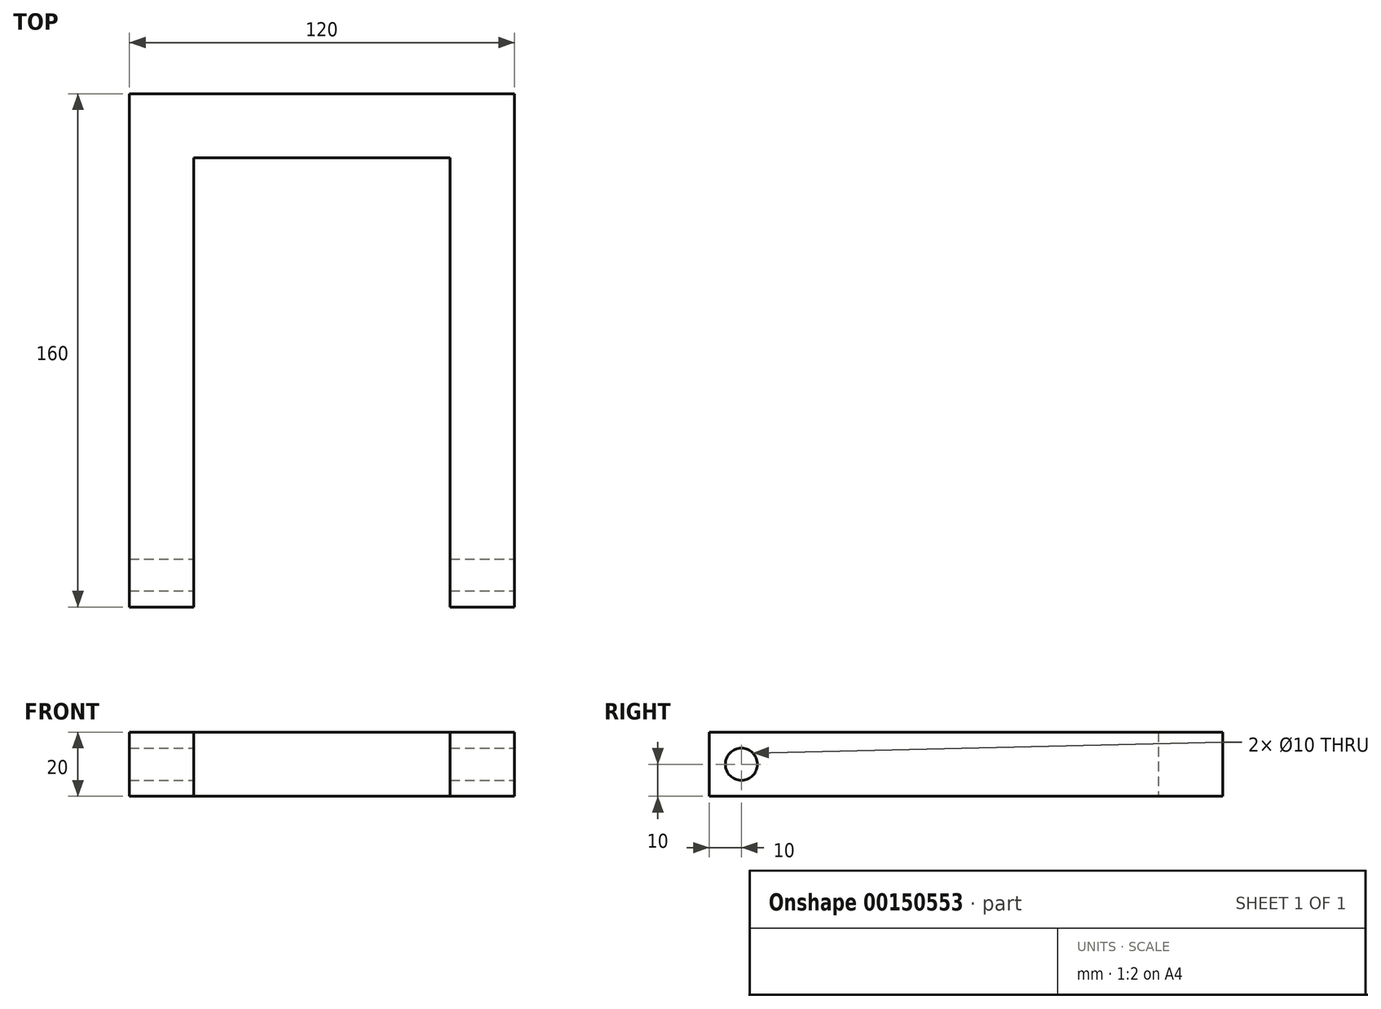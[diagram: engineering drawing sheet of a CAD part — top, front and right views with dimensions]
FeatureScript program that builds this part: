
annotation { "Feature Type Name" : "Feature", "Feature Type Description" : "" }
export const myFeature = defineFeature(function(context is Context, id is Id, definition is map)
    precondition{}
    {
        {
            var Q0;
            Q0=qCreatedBy(makeId("Top.planeOp"),FACE);
            var sketch = newSketch(context, id + "F0", { "sketchPlane" : qUnion([Q0])});
            skLineSegment(sketch, "E0.bottom", {"start": v(60, -80) * mm, "end": v(40, -80) * mm});
            skLineSegment(sketch, "E0.top", {"start": v(60, 80) * mm, "end": v(-60, 80) * mm});
            skLineSegment(sketch, "E0.left", {"start": v(60, -80) * mm, "end": v(60, 80) * mm});
            skLineSegment(sketch, "E0.right", {"start": v(-60, -80) * mm, "end": v(-60, 80) * mm});
            skPoint(sketch, "E0.middle", {"position": v(0, 0) * mm});
            skLineSegment(sketch, "E1.top", {"start": v(40, 60) * mm, "end": v(-40, 60) * mm});
            skLineSegment(sketch, "E1.left", {"start": v(40, -60) * mm, "end": v(40, 60) * mm});
            skLineSegment(sketch, "E1.right", {"start": v(-40, -60) * mm, "end": v(-40, 60) * mm});
            skLineSegment(sketch, "E2", {"start": v(-40, -60) * mm, "end": v(-40, -80) * mm});
            skLineSegment(sketch, "E3", {"start": v(40, -60) * mm, "end": v(40, -80) * mm});
            skLineSegment(sketch, "E4.trimOffspring", {"start": v(-40, -80) * mm, "end": v(-60, -80) * mm});
            skSolve(sketch);
        }
        {
            var Q0;
            Q0 = qSketchRegion(id + "F0", true);
            extrude(context, id + "F1", {"entities" : qUnion([Q0]), "endBound" : BoundingType.SYMMETRIC, "depth" : 20 * mm});
        }
        {
            var Q0;
            Q0=qCreatedBy(makeId("Right.planeOp"),FACE);
            var sketch = newSketch(context, id + "F2", { "sketchPlane" : qUnion([Q0])});
            skCircle(sketch, "E5", {"center": v(-70, 0) * mm, "radius": 5 * mm});
            skSolve(sketch);
        }
        {
            var Q0;
            Q0 = qSketchRegion(id + "F2", true);
            extrude(context, id + "F3", {"entities" : qUnion([Q0]), "operationType" : NewBodyOperationType.REMOVE, "endBound" : BoundingType.SYMMETRIC, "oppositeDirection" : true, "depth" : 120 * mm});
        }
    });
